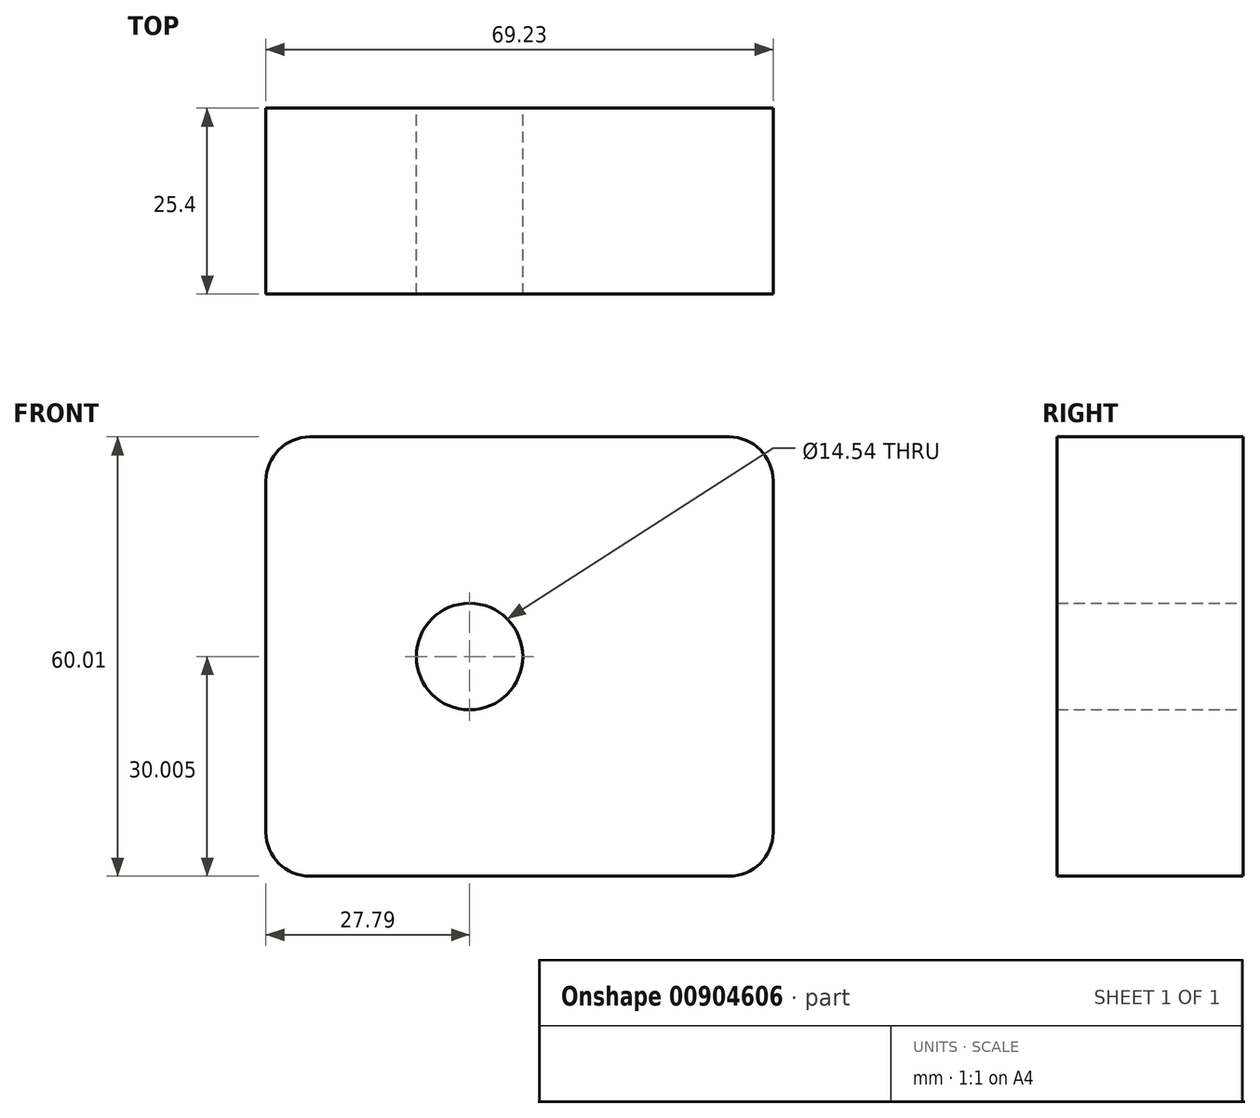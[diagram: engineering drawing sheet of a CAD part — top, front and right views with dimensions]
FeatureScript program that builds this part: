
annotation { "Feature Type Name" : "Feature", "Feature Type Description" : "" }
export const myFeature = defineFeature(function(context is Context, id is Id, definition is map)
    precondition{}
    {
        {
            var Q0;
            Q0=qCreatedBy(makeId("Front.planeOp"),FACE);
            var sketch = newSketch(context, id + "F0", { "sketchPlane" : qUnion([Q0])});
            skLineSegment(sketch, "E0.bottom", {"start": v(-27.79, 60.01) * mm, "end": v(41.44, 60.01) * mm});
            skLineSegment(sketch, "E0.top", {"start": v(-27.79, 0) * mm, "end": v(41.44, 0) * mm});
            skLineSegment(sketch, "E0.left", {"start": v(-27.79, 60.01) * mm, "end": v(-27.79, 0) * mm});
            skLineSegment(sketch, "E0.right", {"start": v(41.44, 60.01) * mm, "end": v(41.44, 0) * mm});
            skSolve(sketch);
        }
        {
            var Q0;
            Q0 = qSketchRegion(id + "F0", true);
            extrude(context, id + "F1", {"entities" : qUnion([Q0]), "depth" : 25.4 * mm, "offsetDistance" : 25.4 * mm});
        }
        {
            var Q0;
            Q0=makeQuery(id+"F1.opExtrude","SWEPT_EDGE",EDGE,{"disambiguationData":[OSD([sQuery(id+"F0.wireOp",EDGE,"E0.bottom"),sQuery(id+"F0.wireOp",EDGE,"E0.right")])]});
            var Q1;
            Q1=makeQuery(id+"F1.opExtrude","SWEPT_EDGE",EDGE,{"disambiguationData":[OSD([sQuery(id+"F0.wireOp",EDGE,"E0.top"),sQuery(id+"F0.wireOp",EDGE,"E0.right")])]});
            var Q2;
            Q2=makeQuery(id+"F1.opExtrude","SWEPT_EDGE",EDGE,{"disambiguationData":[OSD([sQuery(id+"F0.wireOp",EDGE,"E0.bottom"),sQuery(id+"F0.wireOp",EDGE,"E0.left")])]});
            var Q3;
            Q3=makeQuery(id+"F1.opExtrude","SWEPT_EDGE",EDGE,{"disambiguationData":[OSD([sQuery(id+"F0.wireOp",EDGE,"E0.top"),sQuery(id+"F0.wireOp",EDGE,"E0.left")])]});
            fillet(context, id + "F2", {"entities" : qUnion([Q0, Q1, Q2, Q3]), "radius" : 6 * mm, "tangentPropagation" : true, "allowEdgeOverflow" : false});
        }
        {
            var Q0;
            Q0=makeQuery(id+"F1.opExtrude","CAP_FACE",FACE,{"disambiguationData":[OSD([sQuery(id+"F0.wireOp",EDGE,"E0.bottom"),sQuery(id+"F0.wireOp",EDGE,"E0.top"),sQuery(id+"F0.wireOp",EDGE,"E0.left"),sQuery(id+"F0.wireOp",EDGE,"E0.right")])],"isStart":true});
            var sketch = newSketch(context, id + "F3", { "sketchPlane" : qUnion([Q0])});
            skCircle(sketch, "E1", {"center": v(0, 30) * mm, "radius": 7.27 * mm});
            skPoint(sketch, "E2", {"position": v(-41.44, 30) * mm});
            skSolve(sketch);
        }
        {
            var Q0;
            Q0 = qSketchRegion(id + "F3", true);
            extrude(context, id + "F4", {"entities" : qUnion([Q0]), "operationType" : NewBodyOperationType.REMOVE, "endBound" : BoundingType.UP_TO_NEXT, "oppositeDirection" : true, "depth" : 25 * mm, "offsetDistance" : 25 * mm});
        }
    });
